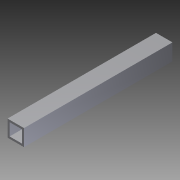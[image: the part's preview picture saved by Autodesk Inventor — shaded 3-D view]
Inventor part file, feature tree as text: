
AUTODESK INVENTOR PART (.ipt)
format: ipt  version: 2012 (Build 160160000, 160)  size: 75,264 bytes
history: native  units: in
note: dims shown in document units (in); Inventor stores cm internally (conversion verified against a paired STEP export)
features: extrude x1, sketch x1
ambient origin geometry x8: Origin, YZ Plane, XZ Plane, XY Plane, X Axis, Y Axis, Z Axis, Center Point
bodies: Solid1 (feature_tree)
feature tree (2):
  extrude  "Extrusion1"  Depth=1.0in
  sketch  "Sketch1"  dims[d0=1.0in d1=1.0in d2=0.125in d3=0.125in d4=0.125in d5=0.125in d6=9.0in d7=0.0in]
